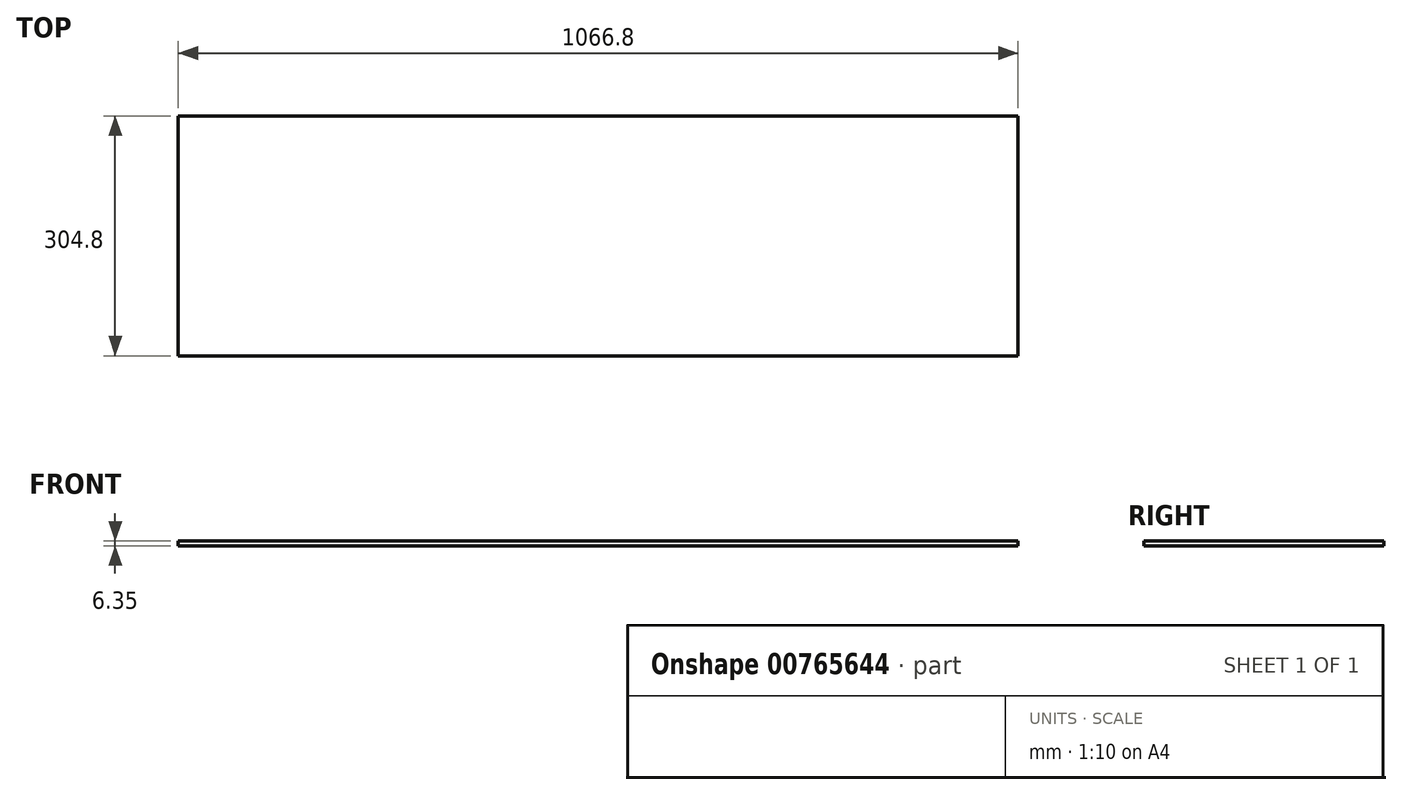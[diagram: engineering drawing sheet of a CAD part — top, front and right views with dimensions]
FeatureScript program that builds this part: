
annotation { "Feature Type Name" : "Feature", "Feature Type Description" : "" }
export const myFeature = defineFeature(function(context is Context, id is Id, definition is map)
    precondition{}
    {
        {
            var Q0;
            Q0=qCreatedBy(makeId("Front.planeOp"),FACE);
            var sketch = newSketch(context, id + "F0", { "sketchPlane" : qUnion([Q0])});
            skLineSegment(sketch, "E0.bottom", {"start": v(-530.7, -463.3) * mm, "end": v(536.1, -463.3) * mm});
            skLineSegment(sketch, "E0.top", {"start": v(-530.7, -469.66) * mm, "end": v(536.1, -469.66) * mm});
            skLineSegment(sketch, "E0.left", {"start": v(-530.7, -463.3) * mm, "end": v(-530.7, -469.66) * mm});
            skLineSegment(sketch, "E0.right", {"start": v(536.1, -463.3) * mm, "end": v(536.1, -469.66) * mm});
            skSolve(sketch);
        }
        {
            var Q0;
            Q0=makeQuery(id+"F0.imprint","IMPRINT",FACE,{"disambiguationData":[TD([[makeQuery(id+"F0.imprint","IMPRINT",EDGE,{"derivedFrom":sQuery(id+"F0.wireOp",EDGE,"E0.bottom")}),-1.0]])]});
            extrude(context, id + "F1", {"entities" : qUnion([Q0]), "depth" : 304.8 * mm, "offsetDistance" : 25.4 * mm});
        }
    });
